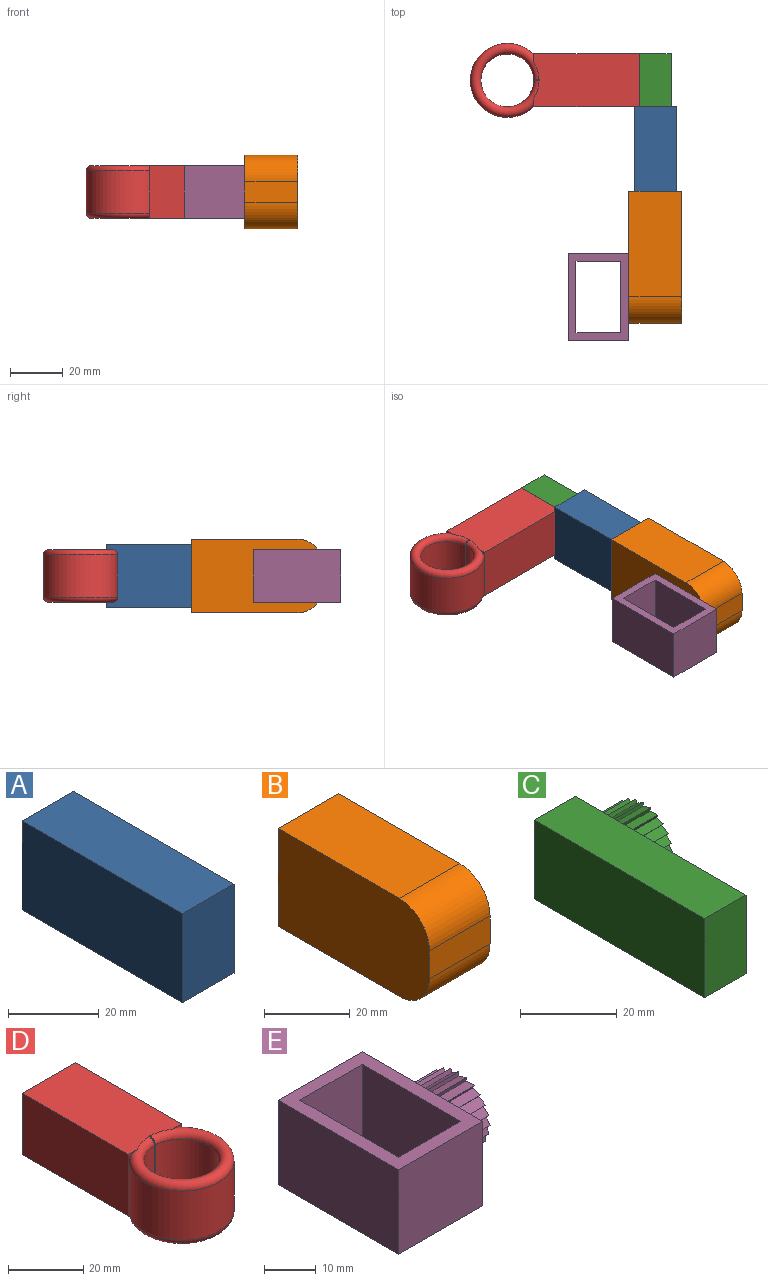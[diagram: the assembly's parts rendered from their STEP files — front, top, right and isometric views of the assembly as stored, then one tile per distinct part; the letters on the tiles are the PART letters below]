
ASSEMBLY  parts=5 mates=4
PART A: 11 faces, bbox 16x50x24 mm
  f0: plane 50x24mm, normal (1,0,0), area 1200mm2, adj f1,f3,f4,f5
  f1: plane 50x16mm, normal (0,0,-1), area 800mm2, adj f0,f2,f4,f5
  f2: plane 50x24mm, normal (-1,0,0), area 1200mm2, adj f1,f3,f4,f5
  f3: plane 50x16mm, normal (0,0,1), area 800mm2, adj f0,f2,f4,f5
  f4: plane 24x16mm, normal (0,1,0), area 131mm2, adj f0,f1,f2,f3,f6,f7,f8,f9
  f5: plane 24x16mm, normal (0,-1,0), area 384mm2, adj f0,f1,f2,f3
  f6: plane 25x20.4mm, normal (-1,0,0), area 510mm2, adj f4,f7,f9,f10
  f7: plane 25x12.4mm, normal (0,0,1), area 310mm2, adj f4,f6,f8,f10
  f8: plane 25x20.4mm, normal (1,0,0), area 510mm2, adj f4,f7,f9,f10
  f9: plane 25x12.4mm, normal (0,0,-1), area 310mm2, adj f4,f6,f8,f10
  f10: plane 20.4x12.4mm, normal (0,1,0), area 253mm2, adj f6,f7,f8,f9
PART B: 62 faces, bbox 20x50x28 mm
  f0: plane 28x20mm, normal (0,1,0), area 159.8mm2, adj f1,f2,f4,f5,f57,f58,f59,f60
  f1: plane 50x28mm, normal (1,0,0), area 1142.7mm2, adj f0,f2,f3,f4,f6,f7,f8,f9
  f2: plane 40x20mm, normal (0,0,1), area 800mm2, adj f0,f1,f5,f55
  f3: plane 20x8mm, normal (0,-1,0), area 160mm2, adj f1,f5,f55,f56
  f4: plane 40x20mm, normal (0,0,-1), area 800mm2, adj f0,f1,f5,f56
  f5: plane 50x28mm, normal (-1,0,0), area 1357.1mm2, adj f0,f2,f3,f4,f55,f56
  f6: plane 10x0.77mm, normal (0,0.71,0.71), area 10.9mm2, adj f1,f7,f53,f54
  f7: plane 10x2.14mm, normal (0,0.46,-0.89), area 24mm2, adj f1,f6,f8,f54
  f8: plane 10x0.95mm, normal (0,0.5,0.87), area 10.9mm2, adj f1,f7,f9,f54
  f9: plane 10x1.78mm, normal (0,0.67,-0.74), area 24mm2, adj f1,f8,f10,f54
  f10: plane 10x1.06mm, normal (0,0.26,0.97), area 10.9mm2, adj f1,f9,f11,f54
  f11: plane 10x2.02mm, normal (0,0.84,-0.54), area 24mm2, adj f1,f10,f12,f54
  f12: plane 10x1.09mm, normal (0,0,1), area 10.9mm2, adj f1,f11,f13,f54
  f13: plane 10x2.29mm, normal (0,0.95,-0.31), area 24mm2, adj f1,f12,f14,f54
  f14: plane 10x1.06mm, normal (0,-0.26,0.97), area 10.9mm2, adj f1,f13,f15,f54
  f15: plane 10x2.4mm, normal (0,1,-0.05), area 24mm2, adj f1,f14,f16,f54
  f16: plane 10x0.95mm, normal (0,-0.5,0.87), area 10.9mm2, adj f1,f15,f17,f54
  f17: plane 10x2.35mm, normal (0,0.98,0.21), area 24mm2, adj f1,f16,f18,f54
  f18: plane 10x0.77mm, normal (0,-0.71,0.71), area 10.9mm2, adj f1,f17,f19,f54
  f19: plane 10x2.14mm, normal (0,0.89,0.46), area 24mm2, adj f1,f18,f20,f54
  f20: plane 10x0.95mm, normal (0,-0.87,0.5), area 10.9mm2, adj f1,f19,f21,f54
  f21: plane 10x1.78mm, normal (0,0.74,0.67), area 24mm2, adj f1,f20,f22,f54
  f22: plane 10x1.06mm, normal (0,-0.97,0.26), area 10.9mm2, adj f1,f21,f23,f54
  f23: plane 10x2.02mm, normal (0,0.54,0.84), area 24mm2, adj f1,f22,f24,f54
  f24: plane 10x1.09mm, normal (0,-1,0), area 10.9mm2, adj f1,f23,f25,f54
  f25: plane 10x2.29mm, normal (0,0.31,0.95), area 24mm2, adj f1,f24,f26,f54
  f26: plane 10x1.06mm, normal (0,-0.97,-0.26), area 10.9mm2, adj f1,f25,f27,f54
  f27: plane 10x2.4mm, normal (0,0.05,1), area 24mm2, adj f1,f26,f28,f54
  f28: plane 10x0.95mm, normal (0,-0.87,-0.5), area 10.9mm2, adj f1,f27,f29,f54
  f29: plane 10x2.35mm, normal (0,-0.21,0.98), area 24mm2, adj f1,f28,f30,f54
  f30: plane 10x0.77mm, normal (0,-0.71,-0.71), area 10.9mm2, adj f1,f29,f31,f54
  f31: plane 10x2.14mm, normal (0,-0.46,0.89), area 24mm2, adj f1,f30,f32,f54
  f32: plane 10x0.95mm, normal (0,-0.5,-0.87), area 10.9mm2, adj f1,f31,f33,f54
  f33: plane 10x1.78mm, normal (0,-0.67,0.74), area 24mm2, adj f1,f32,f34,f54
  f34: plane 10x1.06mm, normal (0,-0.26,-0.97), area 10.9mm2, adj f1,f33,f35,f54
  f35: plane 10x2.02mm, normal (0,-0.84,0.54), area 24mm2, adj f1,f34,f36,f54
  f36: plane 10x1.09mm, normal (0,0,-1), area 10.9mm2, adj f1,f35,f37,f54
  f37: plane 10x2.29mm, normal (0,-0.95,0.31), area 24mm2, adj f1,f36,f38,f54
  f38: plane 10x1.06mm, normal (0,0.26,-0.97), area 10.9mm2, adj f1,f37,f39,f54
  f39: plane 10x2.4mm, normal (0,-1,0.05), area 24mm2, adj f1,f38,f40,f54
  f40: plane 10x0.95mm, normal (0,0.5,-0.87), area 10.9mm2, adj f1,f39,f41,f54
  f41: plane 10x2.35mm, normal (0,-0.98,-0.21), area 24mm2, adj f1,f40,f42,f54
  f42: plane 10x0.77mm, normal (0,0.71,-0.71), area 10.9mm2, adj f1,f41,f43,f54
  f43: plane 10x2.14mm, normal (0,-0.89,-0.46), area 24mm2, adj f1,f42,f44,f54
  f44: plane 10x0.95mm, normal (0,0.87,-0.5), area 10.9mm2, adj f1,f43,f45,f54
  f45: plane 10x1.78mm, normal (0,-0.74,-0.67), area 24mm2, adj f1,f44,f46,f54
  f46: plane 10x1.06mm, normal (0,0.97,-0.26), area 10.9mm2, adj f1,f45,f47,f54
  f47: plane 10x2.02mm, normal (0,-0.54,-0.84), area 24mm2, adj f1,f46,f48,f54
  f48: plane 10x1.09mm, normal (0,1,0), area 10.9mm2, adj f1,f47,f49,f54
  f49: plane 10x2.29mm, normal (0,-0.31,-0.95), area 24mm2, adj f1,f48,f50,f54
  f50: plane 10x1.06mm, normal (0,0.97,0.26), area 10.9mm2, adj f1,f49,f51,f54
  f51: plane 10x2.4mm, normal (0,-0.05,-1), area 24mm2, adj f1,f50,f52,f54
  f52: plane 10x0.95mm, normal (0,0.87,0.5), area 10.9mm2, adj f1,f51,f53,f54
  f53: plane 10x2.35mm, normal (0,0.21,-0.98), area 24mm2, adj f1,f6,f52,f54
  f54: plane 17.74x17.74mm, normal (1,0,0), area 214.3mm2, adj f6,f7,f8,f9,f10,f11,f12,f13
  f55: cylinder r=10mm len=20mm, axis (1,0,0), area 314.2mm2, adj f1,f2,f3,f5
  f56: cylinder r=10mm len=20mm, axis (-1,0,0), area 314.2mm2, adj f1,f3,f4,f5
  f57: plane 25x24.4mm, normal (1,0,0), area 610mm2, adj f0,f58,f60,f61
  f58: plane 25x16.4mm, normal (0,0,-1), area 410mm2, adj f0,f57,f59,f61
  f59: plane 25x24.4mm, normal (-1,0,0), area 610mm2, adj f0,f58,f60,f61
  f60: plane 25x16.4mm, normal (0,0,1), area 410mm2, adj f0,f57,f59,f61
  f61: plane 24.4x16.4mm, normal (0,1,0), area 400.2mm2, adj f57,f58,f59,f60
PART C: 55 faces, bbox 22x50x20 mm
  f0: plane 50x20mm, normal (1,0,0), area 802mm2, adj f1,f3,f4,f5,f6,f7,f8,f9
  f1: plane 50x12mm, normal (0,0,-1), area 600mm2, adj f0,f2,f4,f5
  f2: plane 50x20mm, normal (-1,0,0), area 1000mm2, adj f1,f3,f4,f5
  f3: plane 50x12mm, normal (0,0,1), area 600mm2, adj f0,f2,f4,f5
  f4: plane 20x12mm, normal (0,1,0), area 240mm2, adj f0,f1,f2,f3
  f5: plane 20x12mm, normal (0,-1,0), area 240mm2, adj f0,f1,f2,f3
  f6: plane 10x0.97mm, normal (0,0.97,0.26), area 10mm2, adj f0,f7,f53,f54
  f7: plane 10x2.31mm, normal (0,-0.05,-1), area 23.1mm2, adj f0,f6,f8,f54
  f8: plane 10x0.87mm, normal (0,0.87,0.5), area 10mm2, adj f0,f7,f9,f54
  f9: plane 10x2.26mm, normal (0,0.21,-0.98), area 23.1mm2, adj f0,f8,f10,f54
  f10: plane 10x0.71mm, normal (0,0.71,0.71), area 10mm2, adj f0,f9,f11,f54
  f11: plane 10x2.06mm, normal (0,0.46,-0.89), area 23.1mm2, adj f0,f10,f12,f54
  f12: plane 10x0.87mm, normal (0,0.5,0.87), area 10mm2, adj f0,f11,f13,f54
  f13: plane 10x1.72mm, normal (0,0.67,-0.74), area 23.1mm2, adj f0,f12,f14,f54
  f14: plane 10x0.97mm, normal (0,0.26,0.97), area 10mm2, adj f0,f13,f15,f54
  f15: plane 10x1.94mm, normal (0,0.84,-0.54), area 23.1mm2, adj f0,f14,f16,f54
  f16: plane 10x1mm, normal (0,0,1), area 10mm2, adj f0,f15,f17,f54
  f17: plane 10x2.2mm, normal (0,0.95,-0.31), area 23.1mm2, adj f0,f16,f18,f54
  f18: plane 10x0.97mm, normal (0,-0.26,0.97), area 10mm2, adj f0,f17,f19,f54
  f19: plane 10x2.31mm, normal (0,1,-0.05), area 23.1mm2, adj f0,f18,f20,f54
  f20: plane 10x0.87mm, normal (0,-0.5,0.87), area 10mm2, adj f0,f19,f21,f54
  f21: plane 10x2.26mm, normal (0,0.98,0.21), area 23.1mm2, adj f0,f20,f22,f54
  f22: plane 10x0.71mm, normal (0,-0.71,0.71), area 10mm2, adj f0,f21,f23,f54
  f23: plane 10x2.06mm, normal (0,0.89,0.46), area 23.1mm2, adj f0,f22,f24,f54
  f24: plane 10x0.87mm, normal (0,-0.87,0.5), area 10mm2, adj f0,f23,f25,f54
  f25: plane 10x1.72mm, normal (0,0.74,0.67), area 23.1mm2, adj f0,f24,f26,f54
  f26: plane 10x0.97mm, normal (0,-0.97,0.26), area 10mm2, adj f0,f25,f27,f54
  f27: plane 10x1.94mm, normal (0,0.54,0.84), area 23.1mm2, adj f0,f26,f28,f54
  f28: plane 10x1mm, normal (0,-1,0), area 10mm2, adj f0,f27,f29,f54
  f29: plane 10x2.2mm, normal (0,0.31,0.95), area 23.1mm2, adj f0,f28,f30,f54
  f30: plane 10x0.97mm, normal (0,-0.97,-0.26), area 10mm2, adj f0,f29,f31,f54
  f31: plane 10x2.31mm, normal (0,0.05,1), area 23.1mm2, adj f0,f30,f32,f54
  f32: plane 10x0.87mm, normal (0,-0.87,-0.5), area 10mm2, adj f0,f31,f33,f54
  f33: plane 10x2.26mm, normal (0,-0.21,0.98), area 23.1mm2, adj f0,f32,f34,f54
  f34: plane 10x0.71mm, normal (0,-0.71,-0.71), area 10mm2, adj f0,f33,f35,f54
  f35: plane 10x2.06mm, normal (0,-0.46,0.89), area 23.1mm2, adj f0,f34,f36,f54
  f36: plane 10x0.87mm, normal (0,-0.5,-0.87), area 10mm2, adj f0,f35,f37,f54
  f37: plane 10x1.72mm, normal (0,-0.67,0.74), area 23.1mm2, adj f0,f36,f38,f54
  f38: plane 10x0.97mm, normal (0,-0.26,-0.97), area 10mm2, adj f0,f37,f39,f54
  f39: plane 10x1.94mm, normal (0,-0.84,0.54), area 23.1mm2, adj f0,f38,f40,f54
  f40: plane 10x1mm, normal (0,0,-1), area 10mm2, adj f0,f39,f41,f54
  f41: plane 10x2.2mm, normal (0,-0.95,0.31), area 23.1mm2, adj f0,f40,f42,f54
  f42: plane 10x0.97mm, normal (0,0.26,-0.97), area 10mm2, adj f0,f41,f43,f54
  f43: plane 10x2.31mm, normal (0,-1,0.05), area 23.1mm2, adj f0,f42,f44,f54
  f44: plane 10x0.87mm, normal (0,0.5,-0.87), area 10mm2, adj f0,f43,f45,f54
  f45: plane 10x2.26mm, normal (0,-0.98,-0.21), area 23.1mm2, adj f0,f44,f46,f54
  f46: plane 10x0.71mm, normal (0,0.71,-0.71), area 10mm2, adj f0,f45,f47,f54
  f47: plane 10x2.06mm, normal (0,-0.89,-0.46), area 23.1mm2, adj f0,f46,f48,f54
  f48: plane 10x0.87mm, normal (0,0.87,-0.5), area 10mm2, adj f0,f47,f49,f54
  f49: plane 10x1.72mm, normal (0,-0.74,-0.67), area 23.1mm2, adj f0,f48,f50,f54
  f50: plane 10x0.97mm, normal (0,0.97,-0.26), area 10mm2, adj f0,f49,f51,f54
  f51: plane 10x1.94mm, normal (0,-0.54,-0.84), area 23.1mm2, adj f0,f50,f52,f54
  f52: plane 10x1mm, normal (0,1,0), area 10mm2, adj f0,f51,f53,f54
  f53: plane 10x2.2mm, normal (0,-0.31,-0.95), area 23.1mm2, adj f0,f6,f52,f54
  f54: plane 17x17mm, normal (1,0,0), area 198mm2, adj f6,f7,f8,f9,f10,f11,f12,f13
PART D: 69 faces, bbox 30.3x65.2x20 mm
  f0: plane 16x0.28mm, normal (0,-1,0), area 4.5mm2, adj f60,f63,f64,f68
  f1: plane 20x3.37mm, normal (0,-1,0), area 6.6mm2, adj f2,f3,f4,f57,f59,f65
  f2: plane 40x20mm, normal (0,0,1), area 782mm2, adj f1,f3,f5,f6,f7,f59,f60,f61
  f3: plane 40x20mm, normal (-1,0,0), area 800mm2, adj f1,f2,f4,f7
  f4: plane 40x20mm, normal (0,0,-1), area 782mm2, adj f1,f3,f5,f6,f7,f65,f66,f67
  f5: plane 40x20mm, normal (1,0,0), area 800mm2, adj f2,f4,f6,f7
  f6: plane 20x3.37mm, normal (0,-1,0), area 6.6mm2, adj f2,f4,f5,f57,f59,f65
  f7: plane 20x20mm, normal (0,1,0), area 185.7mm2, adj f2,f3,f4,f5,f8,f9,f10,f11
  f8: plane 10x0.77mm, normal (0.71,0,0.71), area 10.9mm2, adj f7,f9,f55,f56
  f9: plane 10x2.14mm, normal (0.46,0,-0.89), area 24mm2, adj f7,f8,f10,f56
  f10: plane 10x0.95mm, normal (0.5,0,0.87), area 10.9mm2, adj f7,f9,f11,f56
  f11: plane 10x1.78mm, normal (0.67,0,-0.74), area 24mm2, adj f7,f10,f12,f56
  f12: plane 10x1.06mm, normal (0.26,0,0.97), area 10.9mm2, adj f7,f11,f13,f56
  f13: plane 10x2.02mm, normal (0.84,0,-0.54), area 24mm2, adj f7,f12,f14,f56
  f14: plane 10x1.09mm, normal (0,0,1), area 10.9mm2, adj f7,f13,f15,f56
  f15: plane 10x2.29mm, normal (0.95,0,-0.31), area 24mm2, adj f7,f14,f16,f56
  f16: plane 10x1.06mm, normal (-0.26,0,0.97), area 10.9mm2, adj f7,f15,f17,f56
  f17: plane 10x2.4mm, normal (1,0,-0.05), area 24mm2, adj f7,f16,f18,f56
  f18: plane 10x0.95mm, normal (-0.5,0,0.87), area 10.9mm2, adj f7,f17,f19,f56
  f19: plane 10x2.35mm, normal (0.98,0,0.21), area 24mm2, adj f7,f18,f20,f56
  f20: plane 10x0.77mm, normal (-0.71,0,0.71), area 10.9mm2, adj f7,f19,f21,f56
  f21: plane 10x2.14mm, normal (0.89,0,0.46), area 24mm2, adj f7,f20,f22,f56
  f22: plane 10x0.95mm, normal (-0.87,0,0.5), area 10.9mm2, adj f7,f21,f23,f56
  f23: plane 10x1.78mm, normal (0.74,0,0.67), area 24mm2, adj f7,f22,f24,f56
  f24: plane 10x1.06mm, normal (-0.97,0,0.26), area 10.9mm2, adj f7,f23,f25,f56
  f25: plane 10x2.02mm, normal (0.54,0,0.84), area 24mm2, adj f7,f24,f26,f56
  f26: plane 10x1.09mm, normal (-1,0,0), area 10.9mm2, adj f7,f25,f27,f56
  f27: plane 10x2.29mm, normal (0.31,0,0.95), area 24mm2, adj f7,f26,f28,f56
  f28: plane 10x1.06mm, normal (-0.97,0,-0.26), area 10.9mm2, adj f7,f27,f29,f56
  f29: plane 10x2.4mm, normal (0.05,0,1), area 24mm2, adj f7,f28,f30,f56
  f30: plane 10x0.95mm, normal (-0.87,0,-0.5), area 10.9mm2, adj f7,f29,f31,f56
  f31: plane 10x2.35mm, normal (-0.21,0,0.98), area 24mm2, adj f7,f30,f32,f56
  f32: plane 10x0.77mm, normal (-0.71,0,-0.71), area 10.9mm2, adj f7,f31,f33,f56
  f33: plane 10x2.14mm, normal (-0.46,0,0.89), area 24mm2, adj f7,f32,f34,f56
  f34: plane 10x0.95mm, normal (-0.5,0,-0.87), area 10.9mm2, adj f7,f33,f35,f56
  f35: plane 10x1.78mm, normal (-0.67,0,0.74), area 24mm2, adj f7,f34,f36,f56
  f36: plane 10x1.06mm, normal (-0.26,0,-0.97), area 10.9mm2, adj f7,f35,f37,f56
  f37: plane 10x2.02mm, normal (-0.84,0,0.54), area 24mm2, adj f7,f36,f38,f56
  f38: plane 10x1.09mm, normal (0,0,-1), area 10.9mm2, adj f7,f37,f39,f56
  f39: plane 10x2.29mm, normal (-0.95,0,0.31), area 24mm2, adj f7,f38,f40,f56
  f40: plane 10x1.06mm, normal (0.26,0,-0.97), area 10.9mm2, adj f7,f39,f41,f56
  f41: plane 10x2.4mm, normal (-1,0,0.05), area 24mm2, adj f7,f40,f42,f56
  f42: plane 10x0.95mm, normal (0.5,0,-0.87), area 10.9mm2, adj f7,f41,f43,f56
  f43: plane 10x2.35mm, normal (-0.98,0,-0.21), area 24mm2, adj f7,f42,f44,f56
  f44: plane 10x0.77mm, normal (0.71,0,-0.71), area 10.9mm2, adj f7,f43,f45,f56
  f45: plane 10x2.14mm, normal (-0.89,0,-0.46), area 24mm2, adj f7,f44,f46,f56
  f46: plane 10x0.95mm, normal (0.87,0,-0.5), area 10.9mm2, adj f7,f45,f47,f56
  f47: plane 10x1.78mm, normal (-0.74,0,-0.67), area 24mm2, adj f7,f46,f48,f56
  f48: plane 10x1.06mm, normal (0.97,0,-0.26), area 10.9mm2, adj f7,f47,f49,f56
  f49: plane 10x2.02mm, normal (-0.54,0,-0.84), area 24mm2, adj f7,f48,f50,f56
  f50: plane 10x1.09mm, normal (1,0,0), area 10.9mm2, adj f7,f49,f51,f56
  f51: plane 10x2.29mm, normal (-0.31,0,-0.95), area 24mm2, adj f7,f50,f52,f56
  f52: plane 10x1.06mm, normal (0.97,0,0.26), area 10.9mm2, adj f7,f51,f53,f56
  f53: plane 10x2.4mm, normal (-0.05,0,-1), area 24mm2, adj f7,f52,f54,f56
  f54: plane 10x0.95mm, normal (0.87,0,0.5), area 10.9mm2, adj f7,f53,f55,f56
  f55: plane 10x2.35mm, normal (0.21,0,-0.98), area 24mm2, adj f7,f8,f54,f56
  f56: plane 17.74x17.74mm, normal (0,1,0), area 214.3mm2, adj f8,f9,f10,f11,f12,f13,f14,f15
  f57: cylinder r=14mm len=28mm, axis (0,0,1), area 1060.1mm2, adj f1,f6,f59,f65
  f58: cylinder r=10mm len=20mm, axis (0,0,1), area 999.7mm2, adj f59,f63,f64,f65
  f59: torus R=12mm, axis (0,0,1), area 412.8mm2, adj f1,f2,f6,f57,f58,f61,f62
  f60: cylinder r=2mm len=2mm, axis (1,0,0), area 0.9mm2, adj f0,f2,f61,f62
  f61: torus R=4mm, axis (0,0,1), area 0.2mm2, adj f2,f59,f60,f63
  f62: torus R=4mm, axis (0,0,1), area 0.2mm2, adj f2,f59,f60,f64
  f63: cylinder r=2mm len=16mm, axis (0,0,1), area 0.6mm2, adj f0,f58,f61,f66
  f64: cylinder r=2mm len=16mm, axis (0,0,1), area 0.6mm2, adj f0,f58,f62,f67
  f65: torus R=12mm, axis (0,0,1), area 412.8mm2, adj f1,f4,f6,f57,f58,f66,f67
  f66: torus R=4mm, axis (0,0,1), area 0.2mm2, adj f4,f63,f65,f68
  f67: torus R=4mm, axis (0,0,1), area 0.2mm2, adj f4,f64,f65,f68
  f68: cylinder r=2mm len=2mm, axis (-1,0,0), area 0.9mm2, adj f0,f4,f66,f67
PART E: 59 faces, bbox 33x33x20 mm
  f0: plane 27x20mm, normal (1,0,0), area 540mm2, adj f1,f7,f8,f9
  f1: plane 20x17mm, normal (0,-1,0), area 340mm2, adj f0,f2,f8,f9
  f2: plane 27x20mm, normal (-1,0,0), area 540mm2, adj f1,f7,f8,f9
  f3: plane 23x20mm, normal (0,1,0), area 460mm2, adj f4,f6,f8,f9
  f4: plane 33x20mm, normal (-1,0,0), area 660mm2, adj f3,f5,f8,f9
  f5: plane 23x20mm, normal (0,-1,0), area 460mm2, adj f4,f6,f8,f9
  f6: plane 33x20mm, normal (1,0,0), area 462mm2, adj f3,f5,f8,f9,f10,f11,f12,f13
  f7: plane 20x17mm, normal (0,1,0), area 340mm2, adj f0,f2,f8,f9
  f8: plane 33x23mm, normal (0,0,1), area 300mm2, adj f0,f1,f2,f3,f4,f5,f6,f7
  f9: plane 33x23mm, normal (0,0,-1), area 300mm2, adj f0,f1,f2,f3,f4,f5,f6,f7
  f10: plane 10x0.97mm, normal (0,-0.26,0.97), area 10mm2, adj f6,f11,f57,f58
  f11: plane 10x2.31mm, normal (0,1,-0.05), area 23.1mm2, adj f6,f10,f12,f58
  f12: plane 10x0.87mm, normal (0,-0.5,0.87), area 10mm2, adj f6,f11,f13,f58
  f13: plane 10x2.26mm, normal (0,0.98,0.21), area 23.1mm2, adj f6,f12,f14,f58
  f14: plane 10x0.71mm, normal (0,-0.71,0.71), area 10mm2, adj f6,f13,f15,f58
  f15: plane 10x2.06mm, normal (0,0.89,0.46), area 23.1mm2, adj f6,f14,f16,f58
  f16: plane 10x0.87mm, normal (0,-0.87,0.5), area 10mm2, adj f6,f15,f17,f58
  f17: plane 10x1.72mm, normal (0,0.74,0.67), area 23.1mm2, adj f6,f16,f18,f58
  f18: plane 10x0.97mm, normal (0,-0.97,0.26), area 10mm2, adj f6,f17,f19,f58
  f19: plane 10x1.94mm, normal (0,0.54,0.84), area 23.1mm2, adj f6,f18,f20,f58
  f20: plane 10x1mm, normal (0,-1,0), area 10mm2, adj f6,f19,f21,f58
  f21: plane 10x2.2mm, normal (0,0.31,0.95), area 23.1mm2, adj f6,f20,f22,f58
  f22: plane 10x0.97mm, normal (0,-0.97,-0.26), area 10mm2, adj f6,f21,f23,f58
  f23: plane 10x2.31mm, normal (0,0.05,1), area 23.1mm2, adj f6,f22,f24,f58
  f24: plane 10x0.87mm, normal (0,-0.87,-0.5), area 10mm2, adj f6,f23,f25,f58
  f25: plane 10x2.26mm, normal (0,-0.21,0.98), area 23.1mm2, adj f6,f24,f26,f58
  f26: plane 10x0.71mm, normal (0,-0.71,-0.71), area 10mm2, adj f6,f25,f27,f58
  f27: plane 10x2.06mm, normal (0,-0.46,0.89), area 23.1mm2, adj f6,f26,f28,f58
  f28: plane 10x0.87mm, normal (0,-0.5,-0.87), area 10mm2, adj f6,f27,f29,f58
  f29: plane 10x1.72mm, normal (0,-0.67,0.74), area 23.1mm2, adj f6,f28,f30,f58
  f30: plane 10x0.97mm, normal (0,-0.26,-0.97), area 10mm2, adj f6,f29,f31,f58
  f31: plane 10x1.94mm, normal (0,-0.84,0.54), area 23.1mm2, adj f6,f30,f32,f58
  f32: plane 10x1mm, normal (0,0,-1), area 10mm2, adj f6,f31,f33,f58
  f33: plane 10x2.2mm, normal (0,-0.95,0.31), area 23.1mm2, adj f6,f32,f34,f58
  f34: plane 10x0.97mm, normal (0,0.26,-0.97), area 10mm2, adj f6,f33,f35,f58
  f35: plane 10x2.31mm, normal (0,-1,0.05), area 23.1mm2, adj f6,f34,f36,f58
  f36: plane 10x0.87mm, normal (0,0.5,-0.87), area 10mm2, adj f6,f35,f37,f58
  f37: plane 10x2.26mm, normal (0,-0.98,-0.21), area 23.1mm2, adj f6,f36,f38,f58
  f38: plane 10x0.71mm, normal (0,0.71,-0.71), area 10mm2, adj f6,f37,f39,f58
  f39: plane 10x2.06mm, normal (0,-0.89,-0.46), area 23.1mm2, adj f6,f38,f40,f58
  f40: plane 10x0.87mm, normal (0,0.87,-0.5), area 10mm2, adj f6,f39,f41,f58
  f41: plane 10x1.72mm, normal (0,-0.74,-0.67), area 23.1mm2, adj f6,f40,f42,f58
  f42: plane 10x0.97mm, normal (0,0.97,-0.26), area 10mm2, adj f6,f41,f43,f58
  f43: plane 10x1.94mm, normal (0,-0.54,-0.84), area 23.1mm2, adj f6,f42,f44,f58
  f44: plane 10x1mm, normal (0,1,0), area 10mm2, adj f6,f43,f45,f58
  f45: plane 10x2.2mm, normal (0,-0.31,-0.95), area 23.1mm2, adj f6,f44,f46,f58
  f46: plane 10x0.97mm, normal (0,0.97,0.26), area 10mm2, adj f6,f45,f47,f58
  f47: plane 10x2.31mm, normal (0,-0.05,-1), area 23.1mm2, adj f6,f46,f48,f58
  f48: plane 10x0.87mm, normal (0,0.87,0.5), area 10mm2, adj f6,f47,f49,f58
  f49: plane 10x2.26mm, normal (0,0.21,-0.98), area 23.1mm2, adj f6,f48,f50,f58
  f50: plane 10x0.71mm, normal (0,0.71,0.71), area 10mm2, adj f6,f49,f51,f58
  f51: plane 10x2.06mm, normal (0,0.46,-0.89), area 23.1mm2, adj f6,f50,f52,f58
  f52: plane 10x0.87mm, normal (0,0.5,0.87), area 10mm2, adj f6,f51,f53,f58
  f53: plane 10x1.72mm, normal (0,0.67,-0.74), area 23.1mm2, adj f6,f52,f54,f58
  f54: plane 10x0.97mm, normal (0,0.26,0.97), area 10mm2, adj f6,f53,f55,f58
  f55: plane 10x1.94mm, normal (0,0.84,-0.54), area 23.1mm2, adj f6,f54,f56,f58
  f56: plane 10x1mm, normal (0,0,1), area 10mm2, adj f6,f55,f57,f58
  f57: plane 10x2.2mm, normal (0,0.95,-0.31), area 23.1mm2, adj f6,f10,f56,f58
  f58: plane 17x17mm, normal (1,0,0), area 198mm2, adj f10,f11,f12,f13,f14,f15,f16,f17
PLACE A rot(axis=(0,1,0),180deg) t=(-28.38,-33.13,24.07)mm
PLACE B rot(axis=(0,1,0),180deg) t=(-28.38,-35.31,24.07)mm
PLACE C rot(axis=(0,1,0),180deg) t=(-28.38,-43.36,24.07)mm
PLACE D rot(axis=(0,0,-1),90deg) t=(-44.38,66.64,0.07)mm
PLACE E t=(-71.38,-41.81,0.07)mm
MATE revolute B.f54 <-> E.f58  axis (-1,0,0) through (-38.38,-25.31,10.07)mm
MATE slider A.f5 <-> B.f61  axis (0,-1,0) through (-38.38,-3.13,10.07)mm
MATE revolute C.f54 <-> D.f56  axis (-1,0,0) through (-54.38,56.64,10.07)mm
MATE slider C.f5 <-> A.f10  axis (0,-1,0) through (-38.38,16.64,10.07)mm
